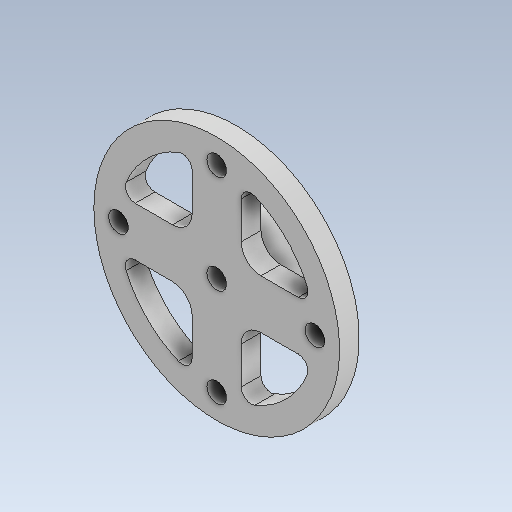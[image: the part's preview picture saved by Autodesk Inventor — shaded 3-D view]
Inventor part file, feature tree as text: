
AUTODESK INVENTOR PART (.ipt)
format: ipt  version: 2023 (Build 270158000, 158)  size: 201,216 bytes
history: native  units: mm
features: sketch x5, other x3
ambient origin geometry x8: Origin, YZ Plane, XZ Plane, XY Plane, X Axis, Y Axis, Z Axis, Center Point
bodies: Solid1 (feature_tree)
feature tree (8):
  other  "tendon_wh_1.ipt"
  other  "Solid1::tendon_wh_1.ipt"
  other  "TaggingFeature1"
  sketch  "Sketch1"  dims[d0=10.0mm]
  sketch  "Sketch2"
  sketch  "Sketch3"
  sketch  "Sketch4"
  sketch  "Sketch5"
